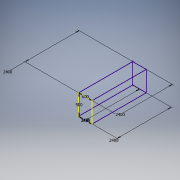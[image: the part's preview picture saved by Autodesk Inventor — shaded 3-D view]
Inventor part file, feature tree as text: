
AUTODESK INVENTOR PART (.ipt)
format: ipt  version: 2016 (Build 200138000, 138)  size: 92,672 bytes
history: native  units: mm
features: sketch x2
ambient origin geometry x8: Origin, YZ Plane, XZ Plane, XY Plane, X Axis, Y Axis, Z Axis, Center Point
feature tree (2):
  sketch  "Boceto1"  dims[d1=600.0mm]
  sketch  "Boceto 3D2"  dims[d2=900.0mm d3=600.0mm d4=2400.0mm d5=2400.0mm d6=2400.0mm d7=2400.0mm]
